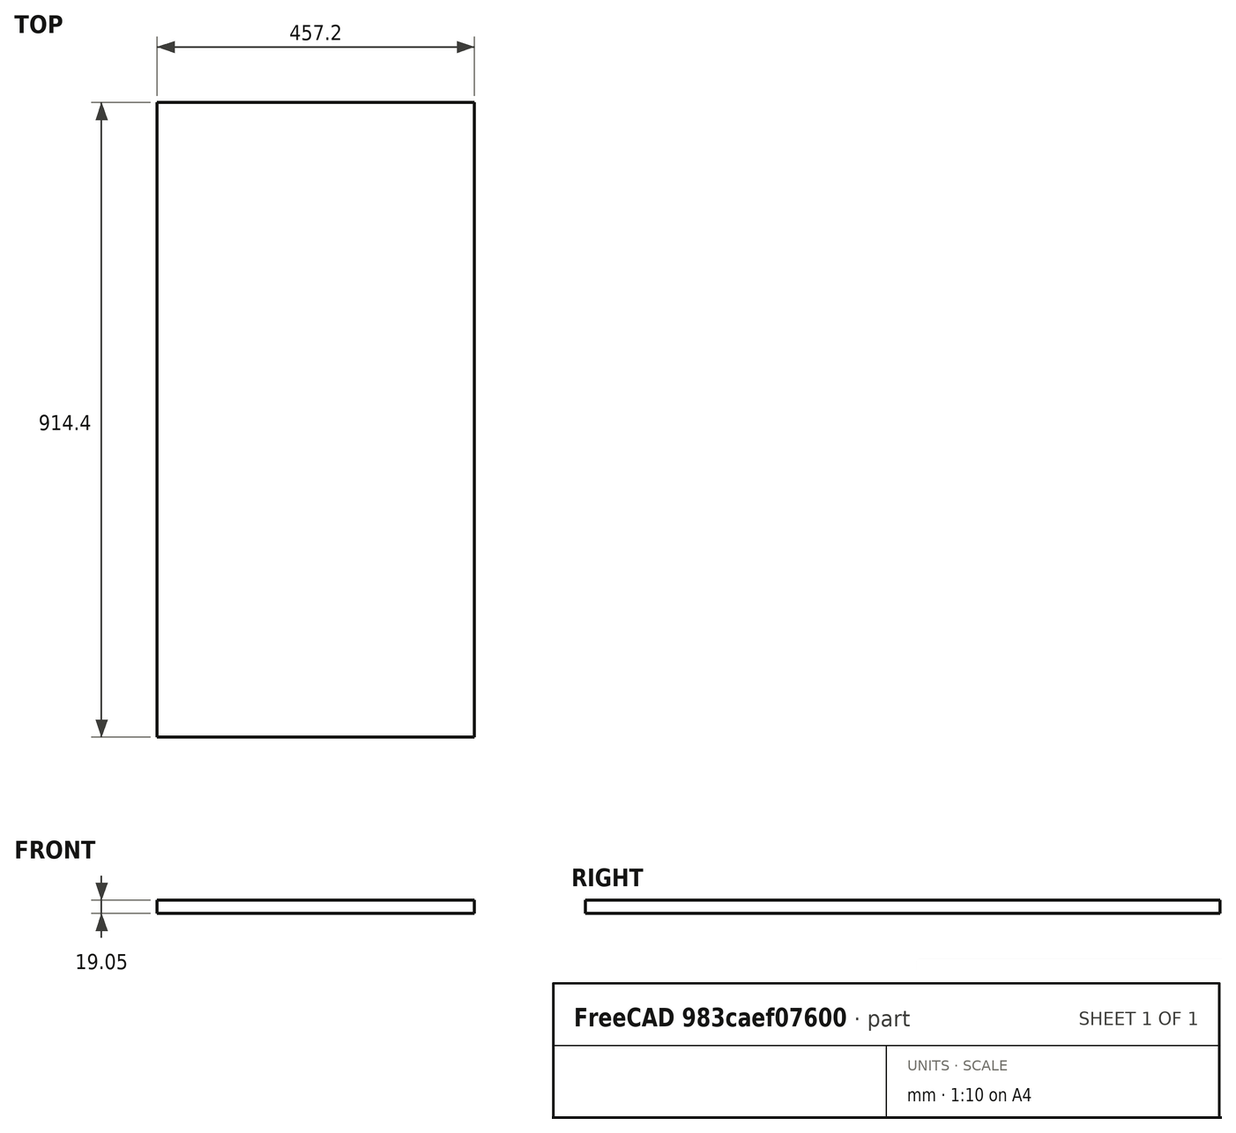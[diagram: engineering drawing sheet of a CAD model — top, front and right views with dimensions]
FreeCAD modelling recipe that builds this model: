
FCSTD DOCUMENT  (FreeCAD 2023.131R26244 +5365 (Git))
Label: woodJoiningPlate
License: All rights reserved
LicenseURL: http://en.wikipedia.org/wiki/All_rights_reserved
objects: Sketcher::SketchObject×1, PartDesign::Pad×1, PartDesign::Body×1, App::Part×1
note: 6 computed .brp shape members not serialized (recipe doc carries the construction recipe); baked Part::Feature solids carry a one-line shape summary decoded from their .brp

FEATURE [Sketcher::SketchObject] Sketch
  ArcFitTolerance = 1e-06
  AttachmentSupport = -> [XY_Plane]
  ExternalBSplineMaxDegree = 5
  ExternalBSplineTolerance = 0.0001
  FixShape = 1
  FullyConstrained = true
  InternalTolerance = 1e-06
  InvalidShape = false
  MakeInternals = false
  MapMode = 5
  Support = -> [XY_Plane]
  TreeRank = 13
  ValidateShape = false
  sketch-geometry (4):
    g0: LineSegment StartX=0 StartY=0 StartZ=0 EndX=457.2 EndY=0 EndZ=0
    g1: LineSegment StartX=457.2 StartY=0 StartZ=0 EndX=457.2 EndY=914.4 EndZ=0
    g2: LineSegment StartX=457.2 StartY=914.4 StartZ=0 EndX=0 EndY=914.4 EndZ=0
    g3: LineSegment StartX=0 StartY=914.4 StartZ=0 EndX=0 EndY=0 EndZ=0
  constraints (11):
    c: Coincident(g0,g1)
    c: Coincident(g1,g2)
    c: Coincident(g2,g3)
    c: Coincident(g3,g0)
    c: Horizontal(g0)
    c: Horizontal(g2)
    c: Vertical(g1)
    c: Vertical(g3)
    c: Coincident(g0,g-1)
    c: DistanceX(g0,g0) = 457.2
    c: DistanceY(g3,g3) = 914.4
FEATURE [PartDesign::Pad] Pad
  AddSubType = 0
  AlongSketchNormal = false
  AutoTaperInnerAngle = true
  CheckUpToFaceLimits = true
  ClaimChildren = false
  Direction = (0,0,1)
  Fit = 0
  FitJoin = 0
  FixShape = 1
  InnerFit = 0
  InnerFitJoin = 0
  InvalidShape = false
  Length = 19.05
  Length2 = 100
  Linearize = true
  NewSolid = false
  Profile = -> Sketch
  Suppress = false
  TaperInnerAngle = 0
  TaperInnerAngleRev = 0
  TreeRank = 14
  Type = 0
  ValidateShape = false
  _ProfileBasedVersion = 1
FEATURE [PartDesign::Body] Body
  AutoGroupSolids = false
  ClaimAllChildren = false
  ExportMode = 0
  FixShape = 1
  Group = -> [Sketch,Pad]
  InvalidShape = false
  Origin = -> Origin001
  Tip = -> Pad
  TreeRank = 12
  ValidateShape = false
  _ExportChildren = -> [Pad]
  _GroupVersion = 1
FEATURE [App::Part] Part  label="woodJoiningPlate-Part"
  ClaimAllChildren = false
  ExportMode = 1
  Group = -> [Body]
  Origin = -> Origin
  TreeRank = 1
  _ExportChildren = -> [Body]
  _GroupVersion = 1
